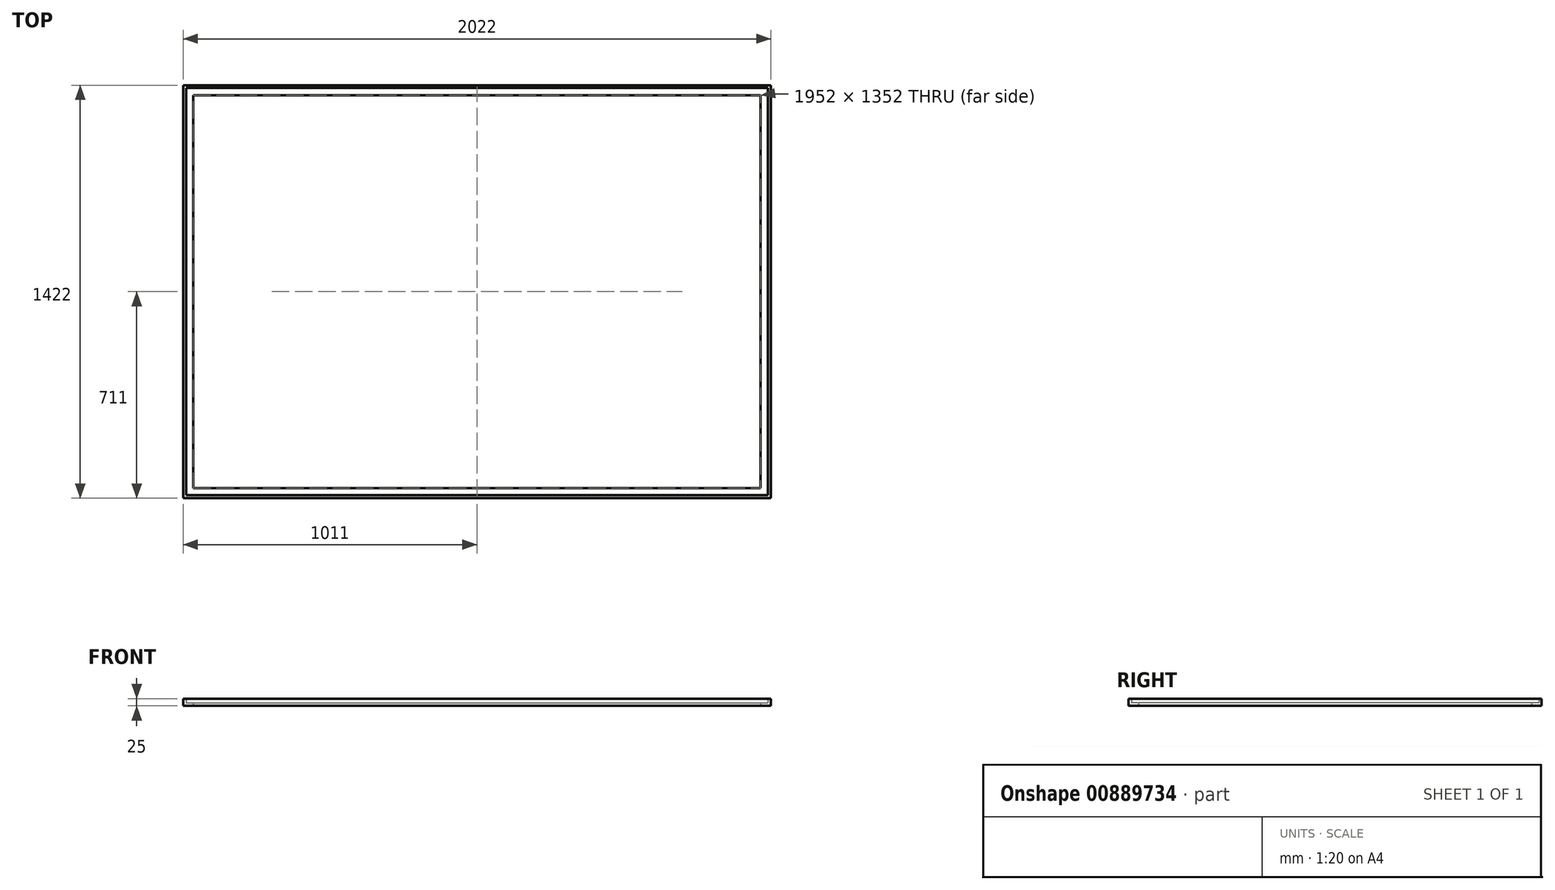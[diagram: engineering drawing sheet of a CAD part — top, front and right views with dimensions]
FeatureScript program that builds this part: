
annotation { "Feature Type Name" : "Feature", "Feature Type Description" : "" }
export const myFeature = defineFeature(function(context is Context, id is Id, definition is map)
    precondition{}
    {
        {
            var Q0;
            Q0=qCreatedBy(makeId("Top.planeOp"),FACE);
            var sketch = newSketch(context, id + "F0", { "sketchPlane" : qUnion([Q0])});
            skLineSegment(sketch, "E0.bottom", {"start": v(-1000, -700) * mm, "end": v(1000, -700) * mm, "construction": true});
            skLineSegment(sketch, "E0.top", {"start": v(-1000, 700) * mm, "end": v(1000, 700) * mm, "construction": true});
            skLineSegment(sketch, "E0.left", {"start": v(-1000, -700) * mm, "end": v(-1000, 700) * mm, "construction": true});
            skLineSegment(sketch, "E0.right", {"start": v(1000, -700) * mm, "end": v(1000, 700) * mm, "construction": true});
            skPoint(sketch, "E0.middle", {"position": v(0, 0) * mm});
            skLineSegment(sketch, "E1.bottom", {"start": v(-976, 676) * mm, "end": v(976, 676) * mm});
            skLineSegment(sketch, "E1.top", {"start": v(-976, -676) * mm, "end": v(976, -676) * mm});
            skLineSegment(sketch, "E1.left", {"start": v(-976, 676) * mm, "end": v(-976, -676) * mm});
            skLineSegment(sketch, "E1.right", {"start": v(976, 676) * mm, "end": v(976, -676) * mm});
            skLineSegment(sketch, "E2.bottom", {"start": v(-1001, 701) * mm, "end": v(1001, 701) * mm});
            skLineSegment(sketch, "E2.top", {"start": v(-1001, -701) * mm, "end": v(1001, -701) * mm});
            skLineSegment(sketch, "E2.left", {"start": v(-1001, 701) * mm, "end": v(-1001, -701) * mm});
            skLineSegment(sketch, "E2.right", {"start": v(1001, 701) * mm, "end": v(1001, -701) * mm});
            skLineSegment(sketch, "E3.bottom", {"start": v(1011, -711) * mm, "end": v(-1011, -711) * mm});
            skLineSegment(sketch, "E3.top", {"start": v(1011, 711) * mm, "end": v(-1011, 711) * mm});
            skLineSegment(sketch, "E3.left", {"start": v(1011, -711) * mm, "end": v(1011, 711) * mm});
            skLineSegment(sketch, "E3.right", {"start": v(-1011, -711) * mm, "end": v(-1011, 711) * mm});
            skLineSegment(sketch, "E4", {"start": v(-1011, -711) * mm, "end": v(-976, -676) * mm});
            skLineSegment(sketch, "E5", {"start": v(-1011, 711) * mm, "end": v(-976, 676) * mm});
            skLineSegment(sketch, "E6", {"start": v(1011, 711) * mm, "end": v(976, 676) * mm});
            skLineSegment(sketch, "E7", {"start": v(1011, -711) * mm, "end": v(976, -676) * mm});
            skSolve(sketch);
        }
        {
            var Q0;
            Q0 = qSketchRegion(id + "F0", true);
            extrude(context, id + "F1", {"entities" : qUnion([Q0]), "depth" : 25 * mm, "offsetDistance" : 25 * mm});
        }
        {
            var Q0;
            {var subQ0=sQuery(id+"F0.wireOp",EDGE,"E1.left");Q0=makeQuery(id+"F0.imprint","IMPRINT",FACE,{"disambiguationData":[TD([[makeQuery(id+"F0.imprint","IMPRINT",EDGE,{"derivedFrom":subQ0}),-1.0]])]});}
            var Q1;
            {var subQ0=sQuery(id+"F0.wireOp",EDGE,"E1.bottom");Q1=makeQuery(id+"F0.imprint","IMPRINT",FACE,{"disambiguationData":[TD([[makeQuery(id+"F0.imprint","IMPRINT",EDGE,{"derivedFrom":subQ0}),1.0]])]});}
            var Q2;
            {var subQ0=sQuery(id+"F0.wireOp",EDGE,"E1.right");Q2=makeQuery(id+"F0.imprint","IMPRINT",FACE,{"disambiguationData":[TD([[makeQuery(id+"F0.imprint","IMPRINT",EDGE,{"derivedFrom":subQ0}),1.0]])]});}
            var Q3;
            {var subQ0=sQuery(id+"F0.wireOp",EDGE,"E1.top");Q3=makeQuery(id+"F0.imprint","IMPRINT",FACE,{"disambiguationData":[TD([[makeQuery(id+"F0.imprint","IMPRINT",EDGE,{"derivedFrom":subQ0}),-1.0]])]});}
            extrude(context, id + "F2", {"entities" : qUnion([Q0, Q1, Q2, Q3]), "operationType" : NewBodyOperationType.ADD, "depth" : 10 * mm, "offsetDistance" : 25 * mm});
        }
    });
